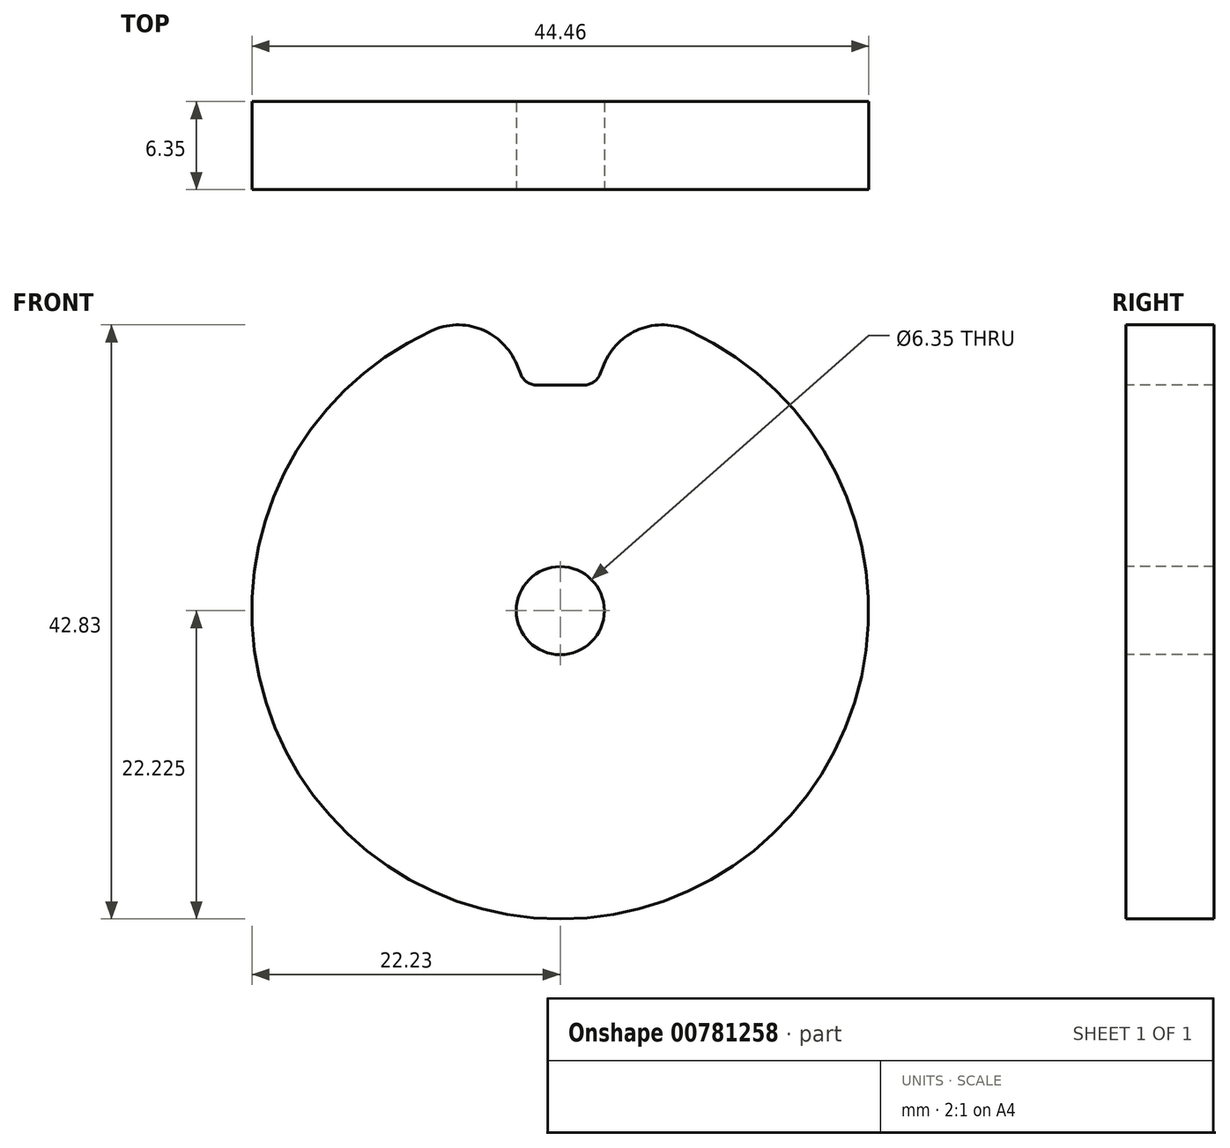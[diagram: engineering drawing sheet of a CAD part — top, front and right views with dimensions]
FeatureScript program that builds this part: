
annotation { "Feature Type Name" : "Feature", "Feature Type Description" : "" }
export const myFeature = defineFeature(function(context is Context, id is Id, definition is map)
    precondition{}
    {
        {
            var Q0;
            Q0=qCreatedBy(makeId("Right.planeOp"),FACE);
            var sketch = newSketch(context, id + "F0", { "sketchPlane" : qUnion([Q0])});
            skLineSegment(sketch, "E0", {"start": v(0, 0) * mm, "end": v(0, 44.45) * mm});
            skLineSegment(sketch, "E1", {"start": v(0, 44.45) * mm, "end": v(6.35, 44.45) * mm});
            skLineSegment(sketch, "E2", {"start": v(6.35, 44.45) * mm, "end": v(6.35, 0) * mm});
            skLineSegment(sketch, "E3", {"start": v(6.35, 0) * mm, "end": v(0, 0) * mm});
            skLineSegment(sketch, "E4", {"start": v(0, 22.23) * mm, "end": v(6.35, 22.23) * mm});
            skSolve(sketch);
        }
        {
            var Q0;
            {var subQ0=sQuery(id+"F0.wireOp",EDGE,"E1");Q0=makeQuery(id+"F0.imprint","IMPRINT",FACE,{"disambiguationData":[TD([[makeQuery(id+"F0.imprint","IMPRINT",EDGE,{"derivedFrom":subQ0}),-1.0]])]});}
            var Q1;
            Q1=sQuery(id+"F0.wireOp",EDGE,"E4");
            revolve(context, id + "F1", {"surfaceOperationType" : NewSurfaceOperationType.NEW, "entities" : qUnion([Q0]), "axis" : qUnion([Q1]), "revolveType" : RevolveType.FULL});
        }
        {
            var Q0;
            Q0=qCreatedBy(makeId("Front.planeOp"),FACE);
            var sketch = newSketch(context, id + "F2", { "sketchPlane" : qUnion([Q0])});
            skLineSegment(sketch, "E5", {"start": v(0, 44.32) * mm, "end": v(0, 38.49) * mm});
            skLineSegment(sketch, "E6.MirrorCS", {"start": v(-2.86, 39.28) * mm, "end": v(-4.92, 44.32) * mm});
            skLineSegment(sketch, "E7.MirrorCS", {"start": v(0, 38.49) * mm, "end": v(-1.69, 38.49) * mm});
            skPoint(sketch, "E8.visualSharp", {"position": v(-2.54, 38.49) * mm});
            skArc(sketch, "E8.filletArc", {"start": v(-2.86, 39.28) * mm, "mid": v(-2.4, 38.7) * mm, "end": v(-1.69, 38.49) * mm});
            skPoint(sketch, "E9.visualSharp", {"position": v(2.54, 38.49) * mm});
            skLineSegment(sketch, "E10", {"start": v(0, 44.32) * mm, "end": v(0, 44.46) * mm});
            skLineSegment(sketch, "E11", {"start": v(-4.92, 44.32) * mm, "end": v(-4.97, 44.46) * mm});
            skLineSegment(sketch, "E12", {"start": v(0, 44.46) * mm, "end": v(-4.97, 44.46) * mm});
            skLineSegment(sketch, "E13.MirrorCS", {"start": v(0, 44.46) * mm, "end": v(4.97, 44.46) * mm});
            skLineSegment(sketch, "E14.MirrorCS", {"start": v(2.86, 39.28) * mm, "end": v(4.92, 44.32) * mm});
            skArc(sketch, "E15.MirrorCS", {"start": v(2.86, 39.28) * mm, "mid": v(2.4, 38.7) * mm, "end": v(1.69, 38.49) * mm});
            skLineSegment(sketch, "E16.MirrorCS", {"start": v(0, 38.49) * mm, "end": v(1.69, 38.49) * mm});
            skLineSegment(sketch, "E17.MirrorCS", {"start": v(4.92, 44.32) * mm, "end": v(4.97, 44.46) * mm});
            skSolve(sketch);
        }
        {
            var Q0;
            Q0=makeQuery(id+"F2.imprint","IMPRINT",FACE,{"disambiguationData":[TD([[makeQuery(id+"F2.imprint","IMPRINT",EDGE,{"derivedFrom":sQuery(id+"F2.wireOp",EDGE,"E5")}),-1.0]])]});
            var Q1;
            Q1=makeQuery(id+"F2.imprint","IMPRINT",FACE,{"disambiguationData":[TD([[makeQuery(id+"F2.imprint","IMPRINT",EDGE,{"derivedFrom":sQuery(id+"F2.wireOp",EDGE,"E5")}),1.0]])]});
            extrude(context, id + "F3", {"entities" : qUnion([Q0, Q1]), "operationType" : NewBodyOperationType.REMOVE, "oppositeDirection" : true, "depth" : 6.35 * mm, "offsetDistance" : 25.4 * mm});
        }
        {
            var Q0;
            {var subQ0=sQuery(id+"F2.wireOp",EDGE,"E11");var subQ1=sQuery(id+"F2.wireOp",EDGE,"E6.MirrorCS");var subQ4=makeQuery(id+"F3.boolean.opBoolean","COPY",FACE,{"derivedFrom":makeQuery(id+"F3.opExtrude","SWEPT_FACE",FACE,{"disambiguationData":[OSD([subQ1,subQ0])]})});Q0=makeQuery(id+"FEMV1dwcXdidpUb_1.7.F3.boolean.opBoolean","INTERSECT",EDGE,{"derivedFrom":[makeQuery(id+"FEMV1dwcXdidpUb_1.6.F3.boolean.opBoolean","SPLIT",FACE,{"disambiguationData":[TD([subQ4])],"derivedFrom":makeQuery(id+"FEMV1dwcXdidpUb_1.5.F3.boolean.opBoolean","SPLIT",FACE,{"disambiguationData":[TD([subQ4])],"derivedFrom":makeQuery(id+"FEMV1dwcXdidpUb_1.4.F3.boolean.opBoolean","SPLIT",FACE,{"disambiguationData":[TD([subQ4])],"derivedFrom":makeQuery(id+"FEMV1dwcXdidpUb_1.3.F3.boolean.opBoolean","SPLIT",FACE,{"disambiguationData":[TD([subQ4])],"derivedFrom":makeQuery(id+"FEMV1dwcXdidpUb_1.2.F3.boolean.opBoolean","SPLIT",FACE,{"disambiguationData":[TD([subQ4])],"derivedFrom":makeQuery(id+"FEMV1dwcXdidpUb_1.1.F3.boolean.opBoolean","SPLIT",FACE,{"disambiguationData":[TD([subQ4])],"derivedFrom":makeQuery(id+"F1.opRevolve","SWEPT_FACE",FACE,{"disambiguationData":[OSD([sQuery(id+"F0.wireOp",EDGE,"E1")])]})})})})})})}),makeQuery(id+"FEMV1dwcXdidpUb_1.7.F3.opExtrude","SWEPT_FACE",FACE,{"disambiguationData":[OSD([subQ1,subQ0])]})]});}
            var Q1;
            {var subQ0=sQuery(id+"F2.wireOp",EDGE,"E17.MirrorCS");var subQ1=sQuery(id+"F2.wireOp",EDGE,"E14.MirrorCS");var subQ4=makeQuery(id+"F3.boolean.opBoolean","COPY",FACE,{"derivedFrom":makeQuery(id+"F3.opExtrude","SWEPT_FACE",FACE,{"disambiguationData":[OSD([sQuery(id+"F2.wireOp",EDGE,"E6.MirrorCS"),sQuery(id+"F2.wireOp",EDGE,"E11")])]})});Q1=makeQuery(id+"FEMV1dwcXdidpUb_1.7.F3.boolean.opBoolean","INTERSECT",EDGE,{"derivedFrom":[makeQuery(id+"FEMV1dwcXdidpUb_1.6.F3.boolean.opBoolean","SPLIT",FACE,{"disambiguationData":[TD([subQ4])],"derivedFrom":makeQuery(id+"FEMV1dwcXdidpUb_1.5.F3.boolean.opBoolean","SPLIT",FACE,{"disambiguationData":[TD([subQ4])],"derivedFrom":makeQuery(id+"FEMV1dwcXdidpUb_1.4.F3.boolean.opBoolean","SPLIT",FACE,{"disambiguationData":[TD([subQ4])],"derivedFrom":makeQuery(id+"FEMV1dwcXdidpUb_1.3.F3.boolean.opBoolean","SPLIT",FACE,{"disambiguationData":[TD([subQ4])],"derivedFrom":makeQuery(id+"FEMV1dwcXdidpUb_1.2.F3.boolean.opBoolean","SPLIT",FACE,{"disambiguationData":[TD([subQ4])],"derivedFrom":makeQuery(id+"FEMV1dwcXdidpUb_1.1.F3.boolean.opBoolean","SPLIT",FACE,{"disambiguationData":[TD([subQ4])],"derivedFrom":makeQuery(id+"F1.opRevolve","SWEPT_FACE",FACE,{"disambiguationData":[OSD([sQuery(id+"F0.wireOp",EDGE,"E1")])]})})})})})})}),makeQuery(id+"FEMV1dwcXdidpUb_1.7.F3.opExtrude","SWEPT_FACE",FACE,{"disambiguationData":[OSD([subQ1,subQ0])]})]});}
            var Q2;
            Q2=makeQuery(id+"F3.boolean.opBoolean","INTERSECT",EDGE,{"derivedFrom":[makeQuery(id+"F1.opRevolve","SWEPT_FACE",FACE,{"disambiguationData":[OSD([sQuery(id+"F0.wireOp",EDGE,"E1")])]}),makeQuery(id+"F3.opExtrude","SWEPT_FACE",FACE,{"disambiguationData":[OSD([sQuery(id+"F2.wireOp",EDGE,"E6.MirrorCS"),sQuery(id+"F2.wireOp",EDGE,"E11")])]})]});
            var Q3;
            Q3=makeQuery(id+"F3.boolean.opBoolean","INTERSECT",EDGE,{"derivedFrom":[makeQuery(id+"F1.opRevolve","SWEPT_FACE",FACE,{"disambiguationData":[OSD([sQuery(id+"F0.wireOp",EDGE,"E1")])]}),makeQuery(id+"F3.opExtrude","SWEPT_FACE",FACE,{"disambiguationData":[OSD([sQuery(id+"F2.wireOp",EDGE,"E14.MirrorCS"),sQuery(id+"F2.wireOp",EDGE,"E17.MirrorCS")])]})]});
            var Q4;
            Q4=makeQuery(id+"FEMV1dwcXdidpUb_1.1.F3.boolean.opBoolean","INTERSECT",EDGE,{"derivedFrom":[makeQuery(id+"F1.opRevolve","SWEPT_FACE",FACE,{"disambiguationData":[OSD([sQuery(id+"F0.wireOp",EDGE,"E1")])]}),makeQuery(id+"FEMV1dwcXdidpUb_1.1.F3.opExtrude","SWEPT_FACE",FACE,{"disambiguationData":[OSD([sQuery(id+"F2.wireOp",EDGE,"E6.MirrorCS"),sQuery(id+"F2.wireOp",EDGE,"E11")])]})]});
            var Q5;
            Q5=makeQuery(id+"FEMV1dwcXdidpUb_1.1.F3.boolean.opBoolean","INTERSECT",EDGE,{"derivedFrom":[makeQuery(id+"F1.opRevolve","SWEPT_FACE",FACE,{"disambiguationData":[OSD([sQuery(id+"F0.wireOp",EDGE,"E1")])]}),makeQuery(id+"FEMV1dwcXdidpUb_1.1.F3.opExtrude","SWEPT_FACE",FACE,{"disambiguationData":[OSD([sQuery(id+"F2.wireOp",EDGE,"E14.MirrorCS"),sQuery(id+"F2.wireOp",EDGE,"E17.MirrorCS")])]})]});
            var Q6;
            {var subQ0=sQuery(id+"F2.wireOp",EDGE,"E11");var subQ1=sQuery(id+"F2.wireOp",EDGE,"E6.MirrorCS");Q6=makeQuery(id+"FEMV1dwcXdidpUb_1.2.F3.boolean.opBoolean","INTERSECT",EDGE,{"derivedFrom":[makeQuery(id+"FEMV1dwcXdidpUb_1.1.F3.boolean.opBoolean","SPLIT",FACE,{"disambiguationData":[TD([makeQuery(id+"F3.boolean.opBoolean","COPY",FACE,{"derivedFrom":makeQuery(id+"F3.opExtrude","SWEPT_FACE",FACE,{"disambiguationData":[OSD([subQ1,subQ0])]})})])],"derivedFrom":makeQuery(id+"F1.opRevolve","SWEPT_FACE",FACE,{"disambiguationData":[OSD([sQuery(id+"F0.wireOp",EDGE,"E1")])]})}),makeQuery(id+"FEMV1dwcXdidpUb_1.2.F3.opExtrude","SWEPT_FACE",FACE,{"disambiguationData":[OSD([subQ1,subQ0])]})]});}
            var Q7;
            {var subQ0=sQuery(id+"F2.wireOp",EDGE,"E17.MirrorCS");var subQ1=sQuery(id+"F2.wireOp",EDGE,"E14.MirrorCS");Q7=makeQuery(id+"FEMV1dwcXdidpUb_1.2.F3.boolean.opBoolean","INTERSECT",EDGE,{"derivedFrom":[makeQuery(id+"FEMV1dwcXdidpUb_1.1.F3.boolean.opBoolean","SPLIT",FACE,{"disambiguationData":[TD([makeQuery(id+"F3.boolean.opBoolean","COPY",FACE,{"derivedFrom":makeQuery(id+"F3.opExtrude","SWEPT_FACE",FACE,{"disambiguationData":[OSD([sQuery(id+"F2.wireOp",EDGE,"E6.MirrorCS"),sQuery(id+"F2.wireOp",EDGE,"E11")])]})})])],"derivedFrom":makeQuery(id+"F1.opRevolve","SWEPT_FACE",FACE,{"disambiguationData":[OSD([sQuery(id+"F0.wireOp",EDGE,"E1")])]})}),makeQuery(id+"FEMV1dwcXdidpUb_1.2.F3.opExtrude","SWEPT_FACE",FACE,{"disambiguationData":[OSD([subQ1,subQ0])]})]});}
            var Q8;
            {var subQ0=sQuery(id+"F2.wireOp",EDGE,"E11");var subQ1=sQuery(id+"F2.wireOp",EDGE,"E6.MirrorCS");var subQ4=makeQuery(id+"F3.boolean.opBoolean","COPY",FACE,{"derivedFrom":makeQuery(id+"F3.opExtrude","SWEPT_FACE",FACE,{"disambiguationData":[OSD([subQ1,subQ0])]})});Q8=makeQuery(id+"FEMV1dwcXdidpUb_1.3.F3.boolean.opBoolean","INTERSECT",EDGE,{"derivedFrom":[makeQuery(id+"FEMV1dwcXdidpUb_1.2.F3.boolean.opBoolean","SPLIT",FACE,{"disambiguationData":[TD([subQ4])],"derivedFrom":makeQuery(id+"FEMV1dwcXdidpUb_1.1.F3.boolean.opBoolean","SPLIT",FACE,{"disambiguationData":[TD([subQ4])],"derivedFrom":makeQuery(id+"F1.opRevolve","SWEPT_FACE",FACE,{"disambiguationData":[OSD([sQuery(id+"F0.wireOp",EDGE,"E1")])]})})}),makeQuery(id+"FEMV1dwcXdidpUb_1.3.F3.opExtrude","SWEPT_FACE",FACE,{"disambiguationData":[OSD([subQ1,subQ0])]})]});}
            var Q9;
            {var subQ0=sQuery(id+"F2.wireOp",EDGE,"E17.MirrorCS");var subQ1=sQuery(id+"F2.wireOp",EDGE,"E14.MirrorCS");var subQ4=makeQuery(id+"F3.boolean.opBoolean","COPY",FACE,{"derivedFrom":makeQuery(id+"F3.opExtrude","SWEPT_FACE",FACE,{"disambiguationData":[OSD([sQuery(id+"F2.wireOp",EDGE,"E6.MirrorCS"),sQuery(id+"F2.wireOp",EDGE,"E11")])]})});Q9=makeQuery(id+"FEMV1dwcXdidpUb_1.3.F3.boolean.opBoolean","INTERSECT",EDGE,{"derivedFrom":[makeQuery(id+"FEMV1dwcXdidpUb_1.2.F3.boolean.opBoolean","SPLIT",FACE,{"disambiguationData":[TD([subQ4])],"derivedFrom":makeQuery(id+"FEMV1dwcXdidpUb_1.1.F3.boolean.opBoolean","SPLIT",FACE,{"disambiguationData":[TD([subQ4])],"derivedFrom":makeQuery(id+"F1.opRevolve","SWEPT_FACE",FACE,{"disambiguationData":[OSD([sQuery(id+"F0.wireOp",EDGE,"E1")])]})})}),makeQuery(id+"FEMV1dwcXdidpUb_1.3.F3.opExtrude","SWEPT_FACE",FACE,{"disambiguationData":[OSD([subQ1,subQ0])]})]});}
            var Q10;
            {var subQ0=sQuery(id+"F2.wireOp",EDGE,"E11");var subQ1=sQuery(id+"F2.wireOp",EDGE,"E6.MirrorCS");var subQ6=makeQuery(id+"F3.boolean.opBoolean","COPY",FACE,{"derivedFrom":makeQuery(id+"F3.opExtrude","SWEPT_FACE",FACE,{"disambiguationData":[OSD([subQ1,subQ0])]})});Q10=makeQuery(id+"FEMV1dwcXdidpUb_1.4.F3.boolean.opBoolean","INTERSECT",EDGE,{"derivedFrom":[makeQuery(id+"FEMV1dwcXdidpUb_1.3.F3.boolean.opBoolean","SPLIT",FACE,{"disambiguationData":[TD([subQ6])],"derivedFrom":makeQuery(id+"FEMV1dwcXdidpUb_1.2.F3.boolean.opBoolean","SPLIT",FACE,{"disambiguationData":[TD([subQ6])],"derivedFrom":makeQuery(id+"FEMV1dwcXdidpUb_1.1.F3.boolean.opBoolean","SPLIT",FACE,{"disambiguationData":[TD([subQ6])],"derivedFrom":makeQuery(id+"F1.opRevolve","SWEPT_FACE",FACE,{"disambiguationData":[OSD([sQuery(id+"F0.wireOp",EDGE,"E1")])]})})})}),makeQuery(id+"FEMV1dwcXdidpUb_1.4.F3.opExtrude","SWEPT_FACE",FACE,{"disambiguationData":[OSD([subQ1,subQ0])]})]});}
            var Q11;
            {var subQ0=sQuery(id+"F2.wireOp",EDGE,"E17.MirrorCS");var subQ1=sQuery(id+"F2.wireOp",EDGE,"E14.MirrorCS");var subQ4=makeQuery(id+"F3.boolean.opBoolean","COPY",FACE,{"derivedFrom":makeQuery(id+"F3.opExtrude","SWEPT_FACE",FACE,{"disambiguationData":[OSD([sQuery(id+"F2.wireOp",EDGE,"E6.MirrorCS"),sQuery(id+"F2.wireOp",EDGE,"E11")])]})});Q11=makeQuery(id+"FEMV1dwcXdidpUb_1.4.F3.boolean.opBoolean","INTERSECT",EDGE,{"derivedFrom":[makeQuery(id+"FEMV1dwcXdidpUb_1.3.F3.boolean.opBoolean","SPLIT",FACE,{"disambiguationData":[TD([subQ4])],"derivedFrom":makeQuery(id+"FEMV1dwcXdidpUb_1.2.F3.boolean.opBoolean","SPLIT",FACE,{"disambiguationData":[TD([subQ4])],"derivedFrom":makeQuery(id+"FEMV1dwcXdidpUb_1.1.F3.boolean.opBoolean","SPLIT",FACE,{"disambiguationData":[TD([subQ4])],"derivedFrom":makeQuery(id+"F1.opRevolve","SWEPT_FACE",FACE,{"disambiguationData":[OSD([sQuery(id+"F0.wireOp",EDGE,"E1")])]})})})}),makeQuery(id+"FEMV1dwcXdidpUb_1.4.F3.opExtrude","SWEPT_FACE",FACE,{"disambiguationData":[OSD([subQ1,subQ0])]})]});}
            var Q12;
            {var subQ0=sQuery(id+"F2.wireOp",EDGE,"E11");var subQ1=sQuery(id+"F2.wireOp",EDGE,"E6.MirrorCS");var subQ6=makeQuery(id+"F3.boolean.opBoolean","COPY",FACE,{"derivedFrom":makeQuery(id+"F3.opExtrude","SWEPT_FACE",FACE,{"disambiguationData":[OSD([subQ1,subQ0])]})});Q12=makeQuery(id+"FEMV1dwcXdidpUb_1.5.F3.boolean.opBoolean","INTERSECT",EDGE,{"derivedFrom":[makeQuery(id+"FEMV1dwcXdidpUb_1.4.F3.boolean.opBoolean","SPLIT",FACE,{"disambiguationData":[TD([subQ6])],"derivedFrom":makeQuery(id+"FEMV1dwcXdidpUb_1.3.F3.boolean.opBoolean","SPLIT",FACE,{"disambiguationData":[TD([subQ6])],"derivedFrom":makeQuery(id+"FEMV1dwcXdidpUb_1.2.F3.boolean.opBoolean","SPLIT",FACE,{"disambiguationData":[TD([subQ6])],"derivedFrom":makeQuery(id+"FEMV1dwcXdidpUb_1.1.F3.boolean.opBoolean","SPLIT",FACE,{"disambiguationData":[TD([subQ6])],"derivedFrom":makeQuery(id+"F1.opRevolve","SWEPT_FACE",FACE,{"disambiguationData":[OSD([sQuery(id+"F0.wireOp",EDGE,"E1")])]})})})})}),makeQuery(id+"FEMV1dwcXdidpUb_1.5.F3.opExtrude","SWEPT_FACE",FACE,{"disambiguationData":[OSD([subQ1,subQ0])]})]});}
            var Q13;
            {var subQ0=sQuery(id+"F2.wireOp",EDGE,"E17.MirrorCS");var subQ1=sQuery(id+"F2.wireOp",EDGE,"E14.MirrorCS");var subQ4=makeQuery(id+"F3.boolean.opBoolean","COPY",FACE,{"derivedFrom":makeQuery(id+"F3.opExtrude","SWEPT_FACE",FACE,{"disambiguationData":[OSD([sQuery(id+"F2.wireOp",EDGE,"E6.MirrorCS"),sQuery(id+"F2.wireOp",EDGE,"E11")])]})});Q13=makeQuery(id+"FEMV1dwcXdidpUb_1.5.F3.boolean.opBoolean","INTERSECT",EDGE,{"derivedFrom":[makeQuery(id+"FEMV1dwcXdidpUb_1.4.F3.boolean.opBoolean","SPLIT",FACE,{"disambiguationData":[TD([subQ4])],"derivedFrom":makeQuery(id+"FEMV1dwcXdidpUb_1.3.F3.boolean.opBoolean","SPLIT",FACE,{"disambiguationData":[TD([subQ4])],"derivedFrom":makeQuery(id+"FEMV1dwcXdidpUb_1.2.F3.boolean.opBoolean","SPLIT",FACE,{"disambiguationData":[TD([subQ4])],"derivedFrom":makeQuery(id+"FEMV1dwcXdidpUb_1.1.F3.boolean.opBoolean","SPLIT",FACE,{"disambiguationData":[TD([subQ4])],"derivedFrom":makeQuery(id+"F1.opRevolve","SWEPT_FACE",FACE,{"disambiguationData":[OSD([sQuery(id+"F0.wireOp",EDGE,"E1")])]})})})})}),makeQuery(id+"FEMV1dwcXdidpUb_1.5.F3.opExtrude","SWEPT_FACE",FACE,{"disambiguationData":[OSD([subQ1,subQ0])]})]});}
            var Q14;
            {var subQ0=sQuery(id+"F2.wireOp",EDGE,"E11");var subQ1=sQuery(id+"F2.wireOp",EDGE,"E6.MirrorCS");var subQ4=makeQuery(id+"F3.boolean.opBoolean","COPY",FACE,{"derivedFrom":makeQuery(id+"F3.opExtrude","SWEPT_FACE",FACE,{"disambiguationData":[OSD([subQ1,subQ0])]})});Q14=makeQuery(id+"FEMV1dwcXdidpUb_1.6.F3.boolean.opBoolean","INTERSECT",EDGE,{"derivedFrom":[makeQuery(id+"FEMV1dwcXdidpUb_1.5.F3.boolean.opBoolean","SPLIT",FACE,{"disambiguationData":[TD([subQ4])],"derivedFrom":makeQuery(id+"FEMV1dwcXdidpUb_1.4.F3.boolean.opBoolean","SPLIT",FACE,{"disambiguationData":[TD([subQ4])],"derivedFrom":makeQuery(id+"FEMV1dwcXdidpUb_1.3.F3.boolean.opBoolean","SPLIT",FACE,{"disambiguationData":[TD([subQ4])],"derivedFrom":makeQuery(id+"FEMV1dwcXdidpUb_1.2.F3.boolean.opBoolean","SPLIT",FACE,{"disambiguationData":[TD([subQ4])],"derivedFrom":makeQuery(id+"FEMV1dwcXdidpUb_1.1.F3.boolean.opBoolean","SPLIT",FACE,{"disambiguationData":[TD([subQ4])],"derivedFrom":makeQuery(id+"F1.opRevolve","SWEPT_FACE",FACE,{"disambiguationData":[OSD([sQuery(id+"F0.wireOp",EDGE,"E1")])]})})})})})}),makeQuery(id+"FEMV1dwcXdidpUb_1.6.F3.opExtrude","SWEPT_FACE",FACE,{"disambiguationData":[OSD([subQ1,subQ0])]})]});}
            var Q15;
            {var subQ0=sQuery(id+"F2.wireOp",EDGE,"E17.MirrorCS");var subQ1=sQuery(id+"F2.wireOp",EDGE,"E14.MirrorCS");var subQ4=makeQuery(id+"F3.boolean.opBoolean","COPY",FACE,{"derivedFrom":makeQuery(id+"F3.opExtrude","SWEPT_FACE",FACE,{"disambiguationData":[OSD([sQuery(id+"F2.wireOp",EDGE,"E6.MirrorCS"),sQuery(id+"F2.wireOp",EDGE,"E11")])]})});Q15=makeQuery(id+"FEMV1dwcXdidpUb_1.6.F3.boolean.opBoolean","INTERSECT",EDGE,{"derivedFrom":[makeQuery(id+"FEMV1dwcXdidpUb_1.5.F3.boolean.opBoolean","SPLIT",FACE,{"disambiguationData":[TD([subQ4])],"derivedFrom":makeQuery(id+"FEMV1dwcXdidpUb_1.4.F3.boolean.opBoolean","SPLIT",FACE,{"disambiguationData":[TD([subQ4])],"derivedFrom":makeQuery(id+"FEMV1dwcXdidpUb_1.3.F3.boolean.opBoolean","SPLIT",FACE,{"disambiguationData":[TD([subQ4])],"derivedFrom":makeQuery(id+"FEMV1dwcXdidpUb_1.2.F3.boolean.opBoolean","SPLIT",FACE,{"disambiguationData":[TD([subQ4])],"derivedFrom":makeQuery(id+"FEMV1dwcXdidpUb_1.1.F3.boolean.opBoolean","SPLIT",FACE,{"disambiguationData":[TD([subQ4])],"derivedFrom":makeQuery(id+"F1.opRevolve","SWEPT_FACE",FACE,{"disambiguationData":[OSD([sQuery(id+"F0.wireOp",EDGE,"E1")])]})})})})})}),makeQuery(id+"FEMV1dwcXdidpUb_1.6.F3.opExtrude","SWEPT_FACE",FACE,{"disambiguationData":[OSD([subQ1,subQ0])]})]});}
            fillet(context, id + "F4", {"entities" : qUnion([Q0, Q1, Q2, Q3, Q4, Q5, Q6, Q7, Q8, Q9, Q10, Q11, Q12, Q13, Q14, Q15]), "radius" : 4.57 * mm, "tangentPropagation" : true, "allowEdgeOverflow" : false});
        }
        {
            var Q0;
            Q0=qCreatedBy(makeId("Front.planeOp"),FACE);
            var sketch = newSketch(context, id + "F5", { "sketchPlane" : qUnion([Q0])});
            skCircle(sketch, "E18", {"center": v(0, 22.23) * mm, "radius": 3.18 * mm});
            skSolve(sketch);
        }
        {
            var Q0;
            Q0=makeQuery(id+"F5.imprint","IMPRINT",FACE,{"disambiguationData":[TD([[makeQuery(id+"F5.imprint","IMPRINT",EDGE,{"derivedFrom":sQuery(id+"F5.wireOp",EDGE,"E18")}),1.0]])]});
            extrude(context, id + "F6", {"entities" : qUnion([Q0]), "operationType" : NewBodyOperationType.REMOVE, "oppositeDirection" : true, "depth" : 6.35 * mm, "offsetDistance" : 25.4 * mm});
        }
    });
